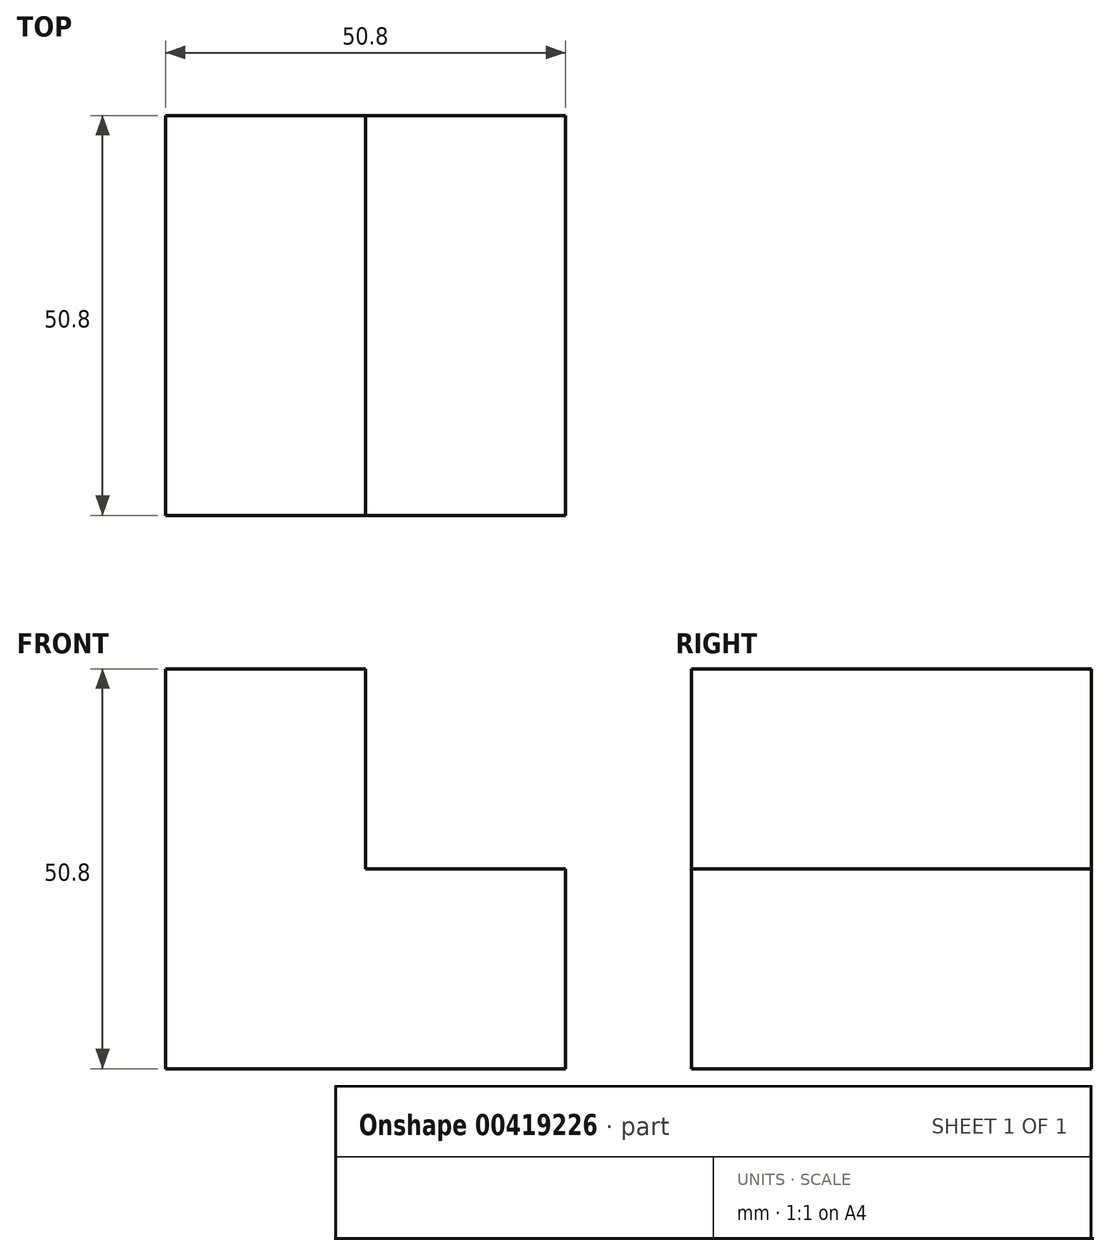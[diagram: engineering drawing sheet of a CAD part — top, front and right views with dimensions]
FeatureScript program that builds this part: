
annotation { "Feature Type Name" : "Feature", "Feature Type Description" : "" }
export const myFeature = defineFeature(function(context is Context, id is Id, definition is map)
    precondition{}
    {
        {
            var Q0;
            Q0=qCreatedBy(makeId("Front.planeOp"),FACE);
            var sketch = newSketch(context, id + "F0", { "sketchPlane" : qUnion([Q0])});
            skLineSegment(sketch, "E0", {"start": v(1.6, 0) * mm, "end": v(0, 0) * mm});
            skLineSegment(sketch, "E1", {"start": v(0, 0) * mm, "end": v(-50.8, 0) * mm});
            skLineSegment(sketch, "E2", {"start": v(-50.8, 0) * mm, "end": v(-50.8, 50.8) * mm});
            skLineSegment(sketch, "E3", {"start": v(-50.8, 50.8) * mm, "end": v(-25.4, 50.8) * mm});
            skLineSegment(sketch, "E4", {"start": v(-25.4, 50.8) * mm, "end": v(-25.4, 25.4) * mm});
            skLineSegment(sketch, "E5", {"start": v(-25.4, 25.4) * mm, "end": v(0, 25.4) * mm});
            skLineSegment(sketch, "E6", {"start": v(0, 25.4) * mm, "end": v(0, 0) * mm});
            skSolve(sketch);
        }
        {
            var Q0;
            Q0=makeQuery(id+"F0.imprint","IMPRINT",FACE,{"disambiguationData":[TD([[makeQuery(id+"F0.imprint","IMPRINT",EDGE,{"derivedFrom":sQuery(id+"F0.wireOp",EDGE,"E1")}),-1.0]])]});
            extrude(context, id + "F1", {"entities" : qUnion([Q0]), "depth" : 50.8 * mm});
        }
    });
